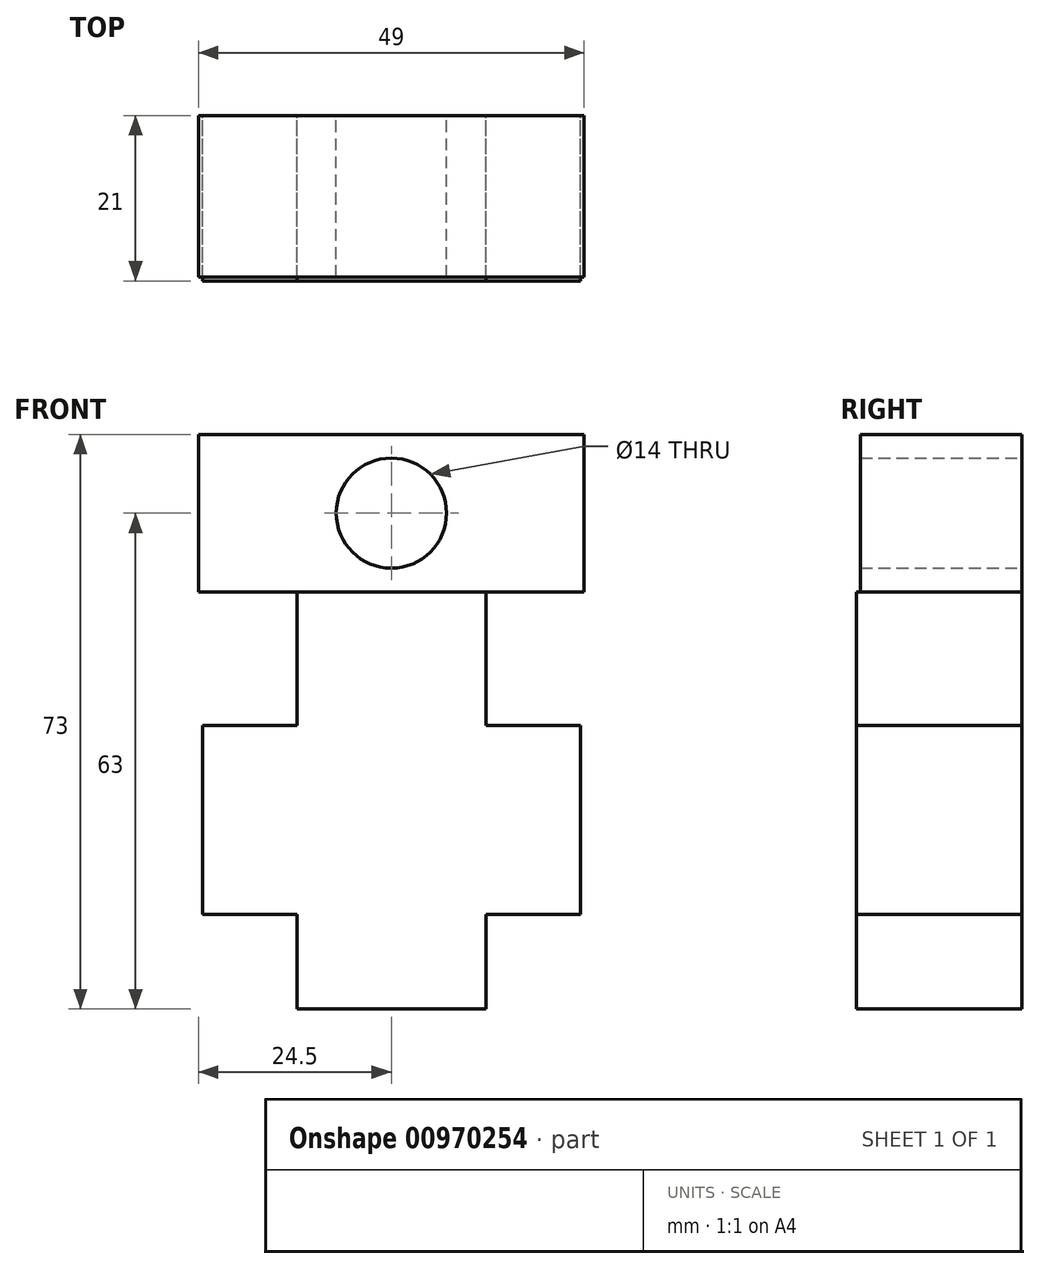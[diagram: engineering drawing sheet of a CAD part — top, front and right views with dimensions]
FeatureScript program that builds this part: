
annotation { "Feature Type Name" : "Feature", "Feature Type Description" : "" }
export const myFeature = defineFeature(function(context is Context, id is Id, definition is map)
    precondition{}
    {
        {
            var Q0;
            Q0=qCreatedBy(makeId("Front.planeOp"),FACE);
            var sketch = newSketch(context, id + "F0", { "sketchPlane" : qUnion([Q0])});
            skLineSegment(sketch, "E0", {"start": v(0, 0) * mm, "end": v(24, 0) * mm});
            skLineSegment(sketch, "E1", {"start": v(24, 0) * mm, "end": v(24, 12) * mm});
            skLineSegment(sketch, "E2", {"start": v(24, 12) * mm, "end": v(36, 12) * mm});
            skLineSegment(sketch, "E3", {"start": v(36, 12) * mm, "end": v(36, 36) * mm});
            skLineSegment(sketch, "E4", {"start": v(36, 36) * mm, "end": v(24, 36) * mm});
            skLineSegment(sketch, "E5", {"start": v(24, 36) * mm, "end": v(24, 53) * mm});
            skLineSegment(sketch, "E6", {"start": v(24, 53) * mm, "end": v(0, 53) * mm});
            skLineSegment(sketch, "E7", {"start": v(0, 53) * mm, "end": v(0, 36) * mm});
            skLineSegment(sketch, "E8", {"start": v(0, 36) * mm, "end": v(-12, 36) * mm});
            skLineSegment(sketch, "E9", {"start": v(-12, 36) * mm, "end": v(-12, 12) * mm});
            skLineSegment(sketch, "E10", {"start": v(-12, 12) * mm, "end": v(0, 12) * mm});
            skLineSegment(sketch, "E11", {"start": v(0, 12) * mm, "end": v(0, 0) * mm});
            skSolve(sketch);
        }
        {
            var Q0;
            Q0=makeQuery(id+"F0.imprint","IMPRINT",FACE,{"disambiguationData":[TD([[makeQuery(id+"F0.imprint","IMPRINT",EDGE,{"derivedFrom":sQuery(id+"F0.wireOp",EDGE,"E0")}),1.0]])]});
            extrude(context, id + "F1", {"entities" : qUnion([Q0]), "depth" : 21 * mm, "offsetDistance" : 25 * mm});
        }
        {
            var Q0;
            Q0=makeQuery(id+"F1.opExtrude","SWEPT_FACE",FACE,{"disambiguationData":[OSD([sQuery(id+"F0.wireOp",EDGE,"E6")])]});
            var sketch = newSketch(context, id + "F2", { "sketchPlane" : qUnion([Q0])});
            skLineSegment(sketch, "E12.bottom", {"start": v(-12.5, -20.5) * mm, "end": v(36.5, -20.5) * mm});
            skLineSegment(sketch, "E12.top", {"start": v(-12.5, -0.5) * mm, "end": v(36.5, -0.5) * mm});
            skLineSegment(sketch, "E12.left", {"start": v(-12.5, -20.5) * mm, "end": v(-12.5, -0.5) * mm});
            skLineSegment(sketch, "E12.right", {"start": v(36.5, -20.5) * mm, "end": v(36.5, -0.5) * mm});
            skPoint(sketch, "E12.middle", {"position": v(12, -10.5) * mm});
            skPoint(sketch, "E12.middle.positionSnap0", {"position": v(12, 0) * mm});
            skPoint(sketch, "E12.middle.positionSnap1", {"position": v(0, -10.5) * mm});
            skPoint(sketch, "E12.centerSnap0", {"position": v(12, 0) * mm});
            skPoint(sketch, "E12.centerSnap1", {"position": v(0, -10.5) * mm});
            skSolve(sketch);
        }
        {
            var Q0;
            {var subQ0=sQuery(id+"F2.wireOp",EDGE,"E12.right");Q0=makeQuery(id+"F2.imprint","IMPRINT",FACE,{"disambiguationData":[TD([[makeQuery(id+"F2.imprint","IMPRINT",EDGE,{"derivedFrom":subQ0}),1.0]])]});}
            var Q1;
            {var subQ0=sQuery(id+"F2.wireOp",EDGE,"E12.bottom");var subQ1=sQuery(id+"F0.wireOp",EDGE,"E6");var subQ2=makeQuery(id+"F1.opExtrude","SWEPT_EDGE",EDGE,{"disambiguationData":[OSD([subQ1,sQuery(id+"F0.wireOp",EDGE,"E7")])]});var subQ3=makeQuery(id+"F2.imprint","INTERSECT",VERTEX,{"derivedFrom":[subQ2,subQ0]});Q1=makeQuery(id+"F2.imprint","IMPRINT",FACE,{"disambiguationData":[TD([[makeQuery(id+"F2.imprint","IMPRINT",EDGE,{"disambiguationData":[TD([[subQ3,-1.0]])],"derivedFrom":subQ0}),1.0]])]});}
            var Q2;
            {var subQ0=sQuery(id+"F2.wireOp",EDGE,"E12.left");Q2=makeQuery(id+"F2.imprint","IMPRINT",FACE,{"disambiguationData":[TD([[makeQuery(id+"F2.imprint","IMPRINT",EDGE,{"derivedFrom":subQ0}),-1.0]])]});}
            extrude(context, id + "F3", {"entities" : qUnion([Q0, Q1, Q2]), "operationType" : NewBodyOperationType.ADD, "depth" : 20 * mm, "offsetDistance" : 25 * mm});
        }
        {
            var Q0;
            Q0=makeQuery(id+"F3.opExtrude","SWEPT_FACE",FACE,{"disambiguationData":[OSD([sQuery(id+"F2.wireOp",EDGE,"E12.top")])]});
            var sketch = newSketch(context, id + "F4", { "sketchPlane" : qUnion([Q0])});
            skSolve(sketch);
        }
        {
            var Q0;
            Q0 = qSketchRegion(id + "F4", true);
            var Q1;
            {var subQ0=sQuery(id+"F2.wireOp",EDGE,"E12.top");Q1=makeQuery(id+"F4.imprint","IMPRINT",FACE,{"disambiguationData":[TD([[makeQuery(id+"F4.imprint","IMPRINT",EDGE,{"derivedFrom":makeQuery(id+"F3.opExtrude","CAP_EDGE",EDGE,{"disambiguationData":[OSD([subQ0])],"isStart":false})}),1.0]])]});}
            extrude(context, id + "F5", {"entities" : qUnion([Q0, Q1]), "operationType" : NewBodyOperationType.ADD, "depth" : 0.5 * mm, "offsetDistance" : 25 * mm});
        }
        {
            var Q0;
            Q0=makeQuery(id+"F5.boolean.opBoolean","MERGE",FACE,{"derivedFrom":[makeQuery(id+"F1.opExtrude","CAP_FACE",FACE,{"disambiguationData":[OSD([sQuery(id+"F0.wireOp",EDGE,"E0"),sQuery(id+"F0.wireOp",EDGE,"E1"),sQuery(id+"F0.wireOp",EDGE,"E2"),sQuery(id+"F0.wireOp",EDGE,"E3"),sQuery(id+"F0.wireOp",EDGE,"E4"),sQuery(id+"F0.wireOp",EDGE,"E5"),sQuery(id+"F0.wireOp",EDGE,"E6"),sQuery(id+"F0.wireOp",EDGE,"E7"),sQuery(id+"F0.wireOp",EDGE,"E8"),sQuery(id+"F0.wireOp",EDGE,"E9"),sQuery(id+"F0.wireOp",EDGE,"E10"),sQuery(id+"F0.wireOp",EDGE,"E11")])],"isStart":true}),makeQuery(id+"F5.opExtrude","CAP_FACE",FACE,{"disambiguationData":[OSD([sQuery(id+"F2.wireOp",EDGE,"E12.top"),sQuery(id+"F2.wireOp",EDGE,"E12.left"),sQuery(id+"F2.wireOp",EDGE,"E12.right")])],"isStart":false})]});
            var sketch = newSketch(context, id + "F6", { "sketchPlane" : qUnion([Q0])});
            skCircle(sketch, "E13", {"center": v(-12, 63) * mm, "radius": 7 * mm});
            skPoint(sketch, "E13.centerSnap0", {"position": v(-12, 73) * mm});
            skPoint(sketch, "E13.centerSnap1", {"position": v(12.5, 63) * mm});
            skSolve(sketch);
        }
        {
            var Q0;
            Q0=makeQuery(id+"F6.imprint","IMPRINT",FACE,{"disambiguationData":[TD([[makeQuery(id+"F6.imprint","IMPRINT",EDGE,{"derivedFrom":sQuery(id+"F6.wireOp",EDGE,"E13")}),1.0]])]});
            extrude(context, id + "F7", {"entities" : qUnion([Q0]), "operationType" : NewBodyOperationType.REMOVE, "oppositeDirection" : true, "depth" : 25 * mm, "offsetDistance" : 25 * mm});
        }
    });
